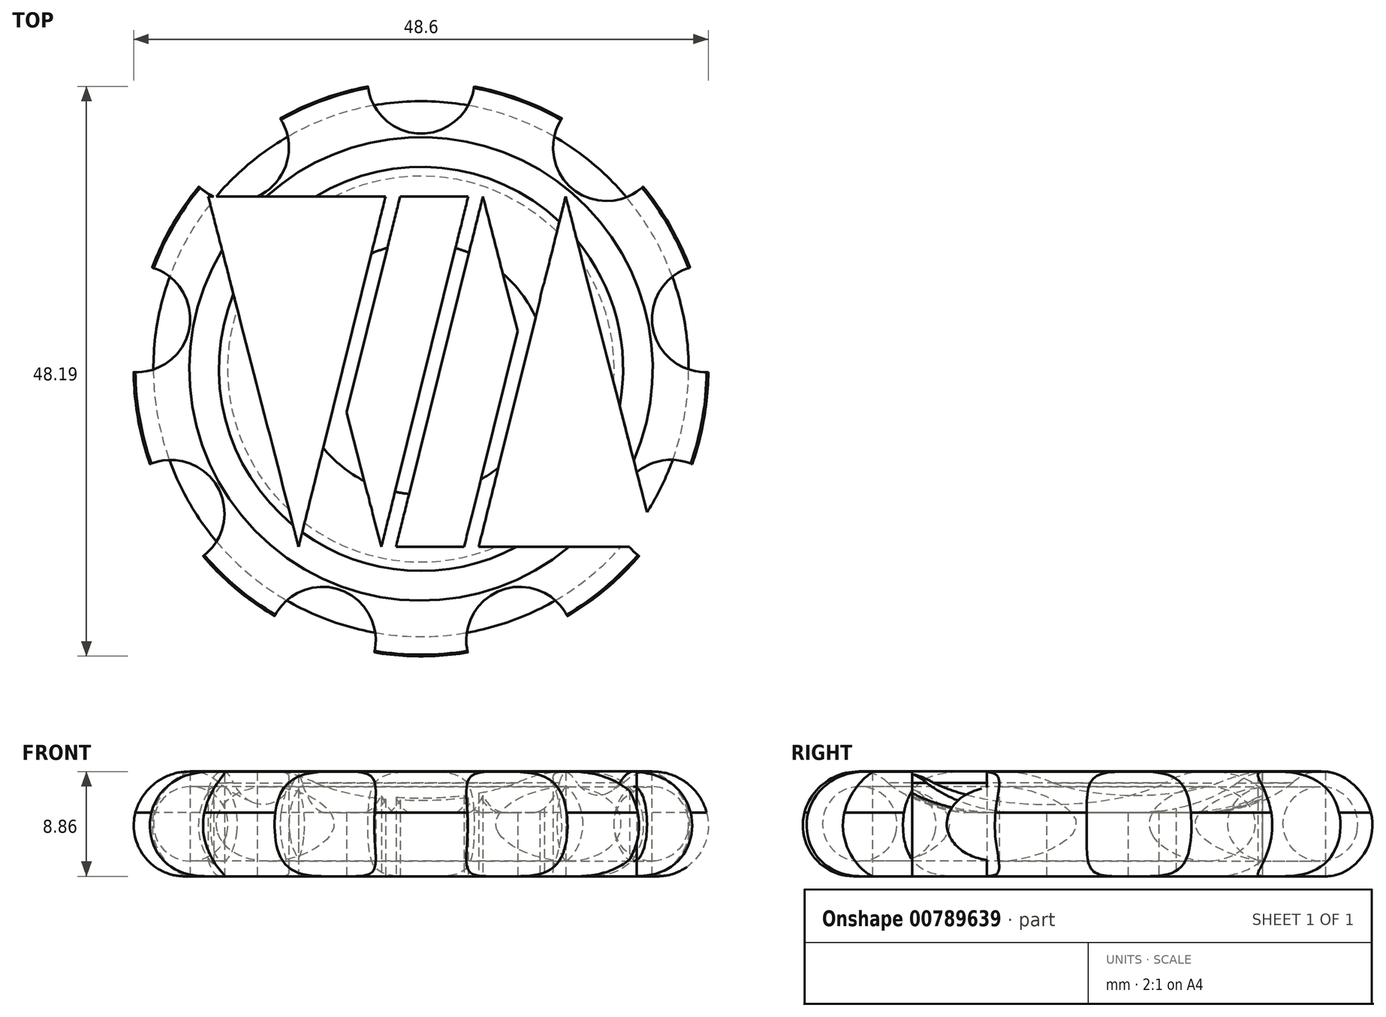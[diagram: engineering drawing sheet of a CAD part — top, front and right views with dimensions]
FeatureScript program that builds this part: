
annotation { "Feature Type Name" : "Feature", "Feature Type Description" : "" }
export const myFeature = defineFeature(function(context is Context, id is Id, definition is map)
    precondition{}
    {
        {
            var Q0;
            Q0=qCreatedBy(makeId("Front.planeOp"),FACE);
            var sketch = newSketch(context, id + "F0", { "sketchPlane" : qUnion([Q0])});
            skLineSegment(sketch, "E0", {"start": v(0, 0) * mm, "end": v(20, 0) * mm});
            skArc(sketch, "E1", {"start": v(20, 0) * mm, "mid": v(23.4, 1.67) * mm, "end": v(24.17, 5.38) * mm});
            skArc(sketch, "E2", {"start": v(24.17, 5.38) * mm, "mid": v(22.47, 7.9) * mm, "end": v(19.6, 8.86) * mm});
            skArc(sketch, "E3", {"start": v(19.6, 8.86) * mm, "mid": v(18.24, 8.64) * mm, "end": v(17.1, 7.9) * mm});
            skArc(sketch, "E4", {"start": v(10.62, 5.38) * mm, "mid": v(14.04, 6.17) * mm, "end": v(17.1, 7.9) * mm});
            skLineSegment(sketch, "E5", {"start": v(10.62, 5.38) * mm, "end": v(0, 5.38) * mm});
            skLineSegment(sketch, "E6.MirrorCS", {"start": v(-10.62, 5.38) * mm, "end": v(0, 5.38) * mm});
            skArc(sketch, "E7.MirrorCS", {"start": v(-10.62, 5.38) * mm, "mid": v(-14.04, 6.17) * mm, "end": v(-17.1, 7.9) * mm});
            skArc(sketch, "E8.MirrorCS", {"start": v(-19.6, 8.86) * mm, "mid": v(-18.24, 8.64) * mm, "end": v(-17.1, 7.9) * mm});
            skArc(sketch, "E9.MirrorCS", {"start": v(-24.17, 5.38) * mm, "mid": v(-22.47, 7.9) * mm, "end": v(-19.6, 8.86) * mm});
            skArc(sketch, "E10.MirrorCS", {"start": v(-20, 0) * mm, "mid": v(-23.4, 1.67) * mm, "end": v(-24.17, 5.38) * mm});
            skLineSegment(sketch, "E11.MirrorCS", {"start": v(0, 0) * mm, "end": v(-20, 0) * mm});
            skLineSegment(sketch, "E12", {"start": v(0, 16.72) * mm, "end": v(0, -8) * mm});
            skSolve(sketch);
        }
        {
            var Q0;
            Q0=makeQuery(id+"F0.imprint","IMPRINT",FACE,{"disambiguationData":[TD([[makeQuery(id+"F0.imprint","IMPRINT",EDGE,{"derivedFrom":sQuery(id+"F0.wireOp",EDGE,"E0")}),1.0]])]});
            var Q1;
            Q1=sQuery(id+"F0.wireOp",EDGE,"E12");
            revolve(context, id + "F1", {"surfaceOperationType" : NewSurfaceOperationType.NEW, "entities" : qUnion([Q0]), "axis" : qUnion([Q1]), "revolveType" : RevolveType.FULL});
        }
        {
            var Q0;
            Q0=qCreatedBy(makeId("Top.planeOp"),FACE);
            var sketch = newSketch(context, id + "F2", { "sketchPlane" : qUnion([Q0])});
            skCircle(sketch, "E13", {"center": v(0, 24.42) * mm, "radius": 4.52 * mm});
            skCircle(sketch, "E14.1.0", {"center": v(-15.7, 18.7) * mm, "radius": 4.52 * mm});
            skCircle(sketch, "E14.2.0", {"center": v(-24.05, 4.24) * mm, "radius": 4.52 * mm});
            skCircle(sketch, "E14.3.0", {"center": v(-21.15, -12.2) * mm, "radius": 4.52 * mm});
            skCircle(sketch, "E14.4.0", {"center": v(-8.35, -22.94) * mm, "radius": 4.52 * mm});
            skCircle(sketch, "E14.5.0", {"center": v(8.35, -22.94) * mm, "radius": 4.52 * mm});
            skCircle(sketch, "E14.6.0", {"center": v(21.15, -12.2) * mm, "radius": 4.52 * mm});
            skCircle(sketch, "E14.7.0", {"center": v(24.05, 4.24) * mm, "radius": 4.52 * mm});
            skCircle(sketch, "E14.8.0", {"center": v(15.7, 18.7) * mm, "radius": 4.52 * mm});
            skPoint(sketch, "E14.center", {"position": v(0, 0) * mm});
            skSolve(sketch);
        }
        {
            var Q0;
            Q0=makeQuery(id+"F2.imprint","IMPRINT",FACE,{"disambiguationData":[TD([[makeQuery(id+"F2.imprint","IMPRINT",EDGE,{"derivedFrom":sQuery(id+"F2.wireOp",EDGE,"E13")}),1.0]])]});
            var Q1;
            Q1=makeQuery(id+"F2.imprint","IMPRINT",FACE,{"disambiguationData":[TD([[makeQuery(id+"F2.imprint","IMPRINT",EDGE,{"derivedFrom":sQuery(id+"F2.wireOp",EDGE,"E14.8.0")}),1.0]])]});
            var Q2;
            Q2=makeQuery(id+"F2.imprint","IMPRINT",FACE,{"disambiguationData":[TD([[makeQuery(id+"F2.imprint","IMPRINT",EDGE,{"derivedFrom":sQuery(id+"F2.wireOp",EDGE,"E14.7.0")}),1.0]])]});
            var Q3;
            Q3=makeQuery(id+"F2.imprint","IMPRINT",FACE,{"disambiguationData":[TD([[makeQuery(id+"F2.imprint","IMPRINT",EDGE,{"derivedFrom":sQuery(id+"F2.wireOp",EDGE,"E14.6.0")}),1.0]])]});
            var Q4;
            Q4=makeQuery(id+"F2.imprint","IMPRINT",FACE,{"disambiguationData":[TD([[makeQuery(id+"F2.imprint","IMPRINT",EDGE,{"derivedFrom":sQuery(id+"F2.wireOp",EDGE,"E14.5.0")}),1.0]])]});
            var Q5;
            Q5=makeQuery(id+"F2.imprint","IMPRINT",FACE,{"disambiguationData":[TD([[makeQuery(id+"F2.imprint","IMPRINT",EDGE,{"derivedFrom":sQuery(id+"F2.wireOp",EDGE,"E14.4.0")}),1.0]])]});
            var Q6;
            Q6=makeQuery(id+"F2.imprint","IMPRINT",FACE,{"disambiguationData":[TD([[makeQuery(id+"F2.imprint","IMPRINT",EDGE,{"derivedFrom":sQuery(id+"F2.wireOp",EDGE,"E14.3.0")}),1.0]])]});
            var Q7;
            Q7=makeQuery(id+"F2.imprint","IMPRINT",FACE,{"disambiguationData":[TD([[makeQuery(id+"F2.imprint","IMPRINT",EDGE,{"derivedFrom":sQuery(id+"F2.wireOp",EDGE,"E14.2.0")}),1.0]])]});
            var Q8;
            Q8=makeQuery(id+"F2.imprint","IMPRINT",FACE,{"disambiguationData":[TD([[makeQuery(id+"F2.imprint","IMPRINT",EDGE,{"derivedFrom":sQuery(id+"F2.wireOp",EDGE,"E14.1.0")}),1.0]])]});
            extrude(context, id + "F3", {"entities" : qUnion([Q0, Q1, Q2, Q3, Q4, Q5, Q6, Q7, Q8]), "operationType" : NewBodyOperationType.REMOVE, "depth" : 25 * mm, "offsetDistance" : 25 * mm});
        }
        {
            var Q0;
            Q0=qCreatedBy(makeId("Top.planeOp"),FACE);
            var sketch = newSketch(context, id + "F4", { "sketchPlane" : qUnion([Q0])});
            skLineSegment(sketch, "E15", {"start": v(-23.46, 14.58) * mm, "end": v(-3, 14.58) * mm, "construction": true});
            skLineSegment(sketch, "E16", {"start": v(-28.13, -15.06) * mm, "end": v(-10.36, -15.06) * mm, "construction": true});
            skLineSegment(sketch, "E17", {"start": v(-18, 14.58) * mm, "end": v(-10.36, -15.06) * mm});
            skLineSegment(sketch, "E18", {"start": v(-10.36, -15.06) * mm, "end": v(-3, 14.58) * mm});
            skLineSegment(sketch, "E19", {"start": v(-1.76, 14.58) * mm, "end": v(4, 14.58) * mm});
            skLineSegment(sketch, "E20", {"start": v(4, 14.58) * mm, "end": v(-3.36, -15.06) * mm});
            skLineSegment(sketch, "E21", {"start": v(-3.36, -15.06) * mm, "end": v(-6.3, -3.67) * mm});
            skLineSegment(sketch, "E22", {"start": v(5.24, 14.58) * mm, "end": v(-2.12, -15.06) * mm});
            skLineSegment(sketch, "E23", {"start": v(5.24, 14.58) * mm, "end": v(8.17, 3.2) * mm});
            skLineSegment(sketch, "E24", {"start": v(4.88, -15.06) * mm, "end": v(12.24, 14.58) * mm});
            skLineSegment(sketch, "E25", {"start": v(12.24, 14.58) * mm, "end": v(19.88, -15.06) * mm});
            skLineSegment(sketch, "E26", {"start": v(-1.76, 14.58) * mm, "end": v(-6.3, -3.67) * mm});
            skLineSegment(sketch, "E27", {"start": v(3.64, -15.06) * mm, "end": v(8.17, 3.2) * mm});
            skLineSegment(sketch, "E28", {"start": v(19.88, -15.06) * mm, "end": v(4.88, -15.06) * mm});
            skLineSegment(sketch, "E29.trimOffspring", {"start": v(-1.76, 14.58) * mm, "end": v(4, 14.58) * mm, "construction": true});
            skPoint(sketch, "E30.orphan", {"position": v(-11, 14.58) * mm});
            skLineSegment(sketch, "E31.trimOffspring", {"start": v(-2.12, -15.06) * mm, "end": v(3.64, -15.06) * mm, "construction": true});
            skLineSegment(sketch, "E32.trimOffspring", {"start": v(4, 14.58) * mm, "end": v(-1.76, 14.58) * mm});
            skLineSegment(sketch, "E33.trimOffspring", {"start": v(3.64, -15.06) * mm, "end": v(-2.12, -15.06) * mm});
            skPoint(sketch, "E34.trimOffspring.end.orphan", {"position": v(12.88, -15.06) * mm});
            skLineSegment(sketch, "E35.trimOffspring", {"start": v(-3, 14.58) * mm, "end": v(-18, 14.58) * mm});
            skArc(sketch, "E36.trimOffspring", {"start": v(10.42, 7.27) * mm, "mid": v(10.2, 6.55) * mm, "end": v(10.06, 5.8) * mm});
            skArc(sketch, "E37.trimOffspring", {"start": v(12.3, 14.32) * mm, "mid": v(12.23, 14.3) * mm, "end": v(12.16, 14.26) * mm});
            skSolve(sketch);
        }
        {
            var Q0;
            Q0=qCreatedBy(makeId("Front.planeOp"),FACE);
            var sketch = newSketch(context, id + "F5", { "sketchPlane" : qUnion([Q0])});
            skCircle(sketch, "E38", {"center": v(-19.49, 4.43) * mm, "radius": 3.15 * mm});
            skLineSegment(sketch, "E39", {"start": v(-19.65, 8.87) * mm, "end": v(-30.64, 8.87) * mm, "construction": true});
            skLineSegment(sketch, "E40", {"start": v(-20.13, 0) * mm, "end": v(-31.8, 0) * mm, "construction": true});
            skSolve(sketch);
        }
        {
            var Q0;
            Q0 = qSketchRegion(id + "F5", true);
            var Q1;
            Q1=sQuery(id+"F0.wireOp",EDGE,"E12");
            revolve(context, id + "F6", {"surfaceOperationType" : NewSurfaceOperationType.NEW, "entities" : qUnion([Q0]), "axis" : qUnion([Q1]), "revolveType" : RevolveType.FULL});
        }
        {
            var Q0;
            Q0 = qSketchRegion(id + "F4", true);
            extrude(context, id + "F7", {"entities" : qUnion([Q0]), "operationType" : NewBodyOperationType.REMOVE, "depth" : 25 * mm, "offsetDistance" : 25 * mm});
        }
    });
